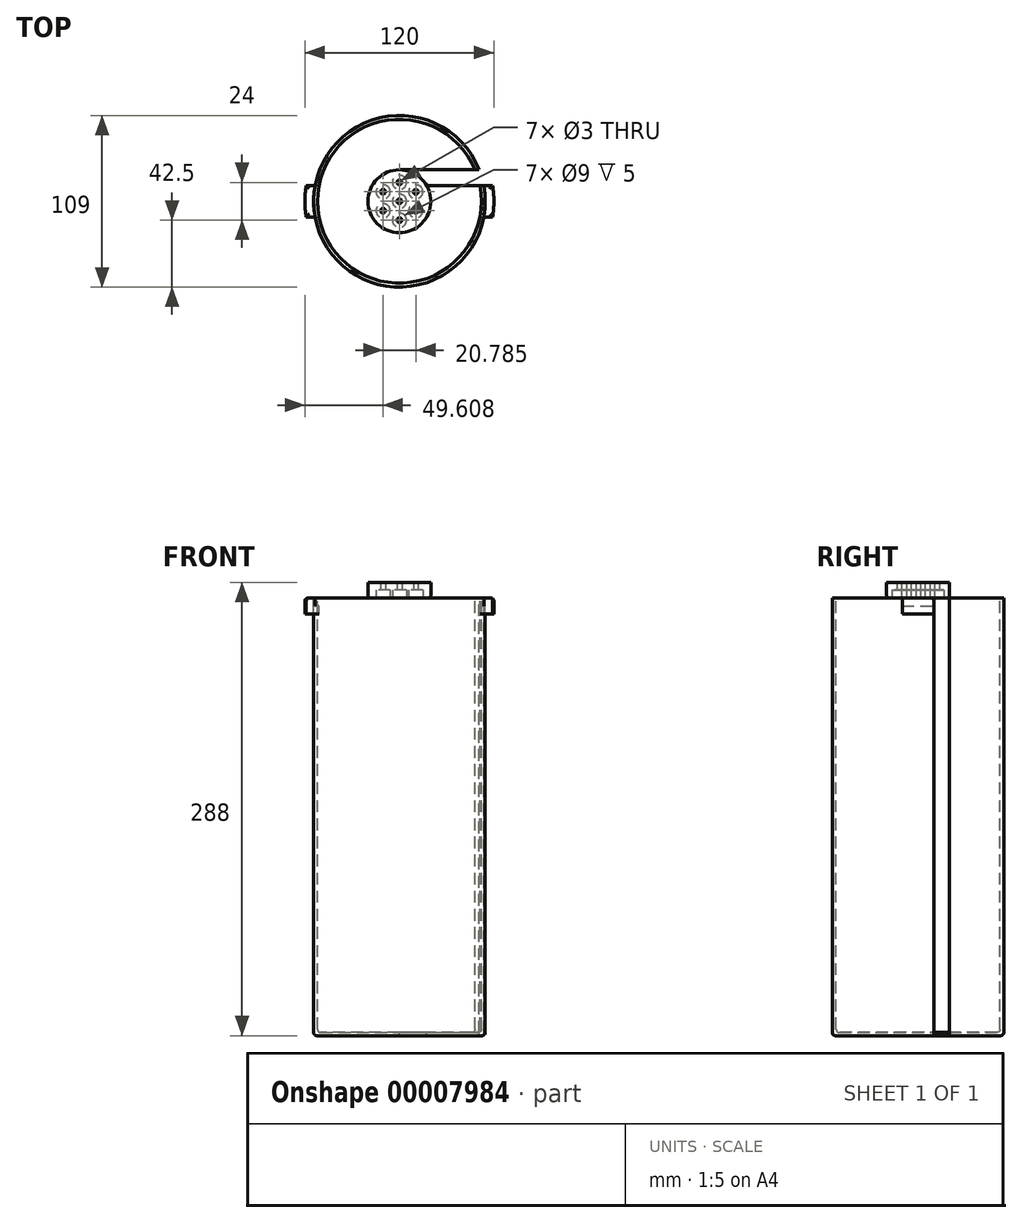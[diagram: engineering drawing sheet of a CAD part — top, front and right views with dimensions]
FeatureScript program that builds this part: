
annotation { "Feature Type Name" : "Feature", "Feature Type Description" : "" }
export const myFeature = defineFeature(function(context is Context, id is Id, definition is map)
    precondition{}
    {
        {
            var Q0;
            Q0=qCreatedBy(makeId("Top.planeOp"),FACE);
            var sketch = newSketch(context, id + "F0", { "sketchPlane" : qUnion([Q0])});
            skCircle(sketch, "E0", {"center": v(0, 0) * mm, "radius": 52 * mm});
            skCircle(sketch, "E1", {"center": v(0, 0) * mm, "radius": 4.5 * mm});
            skCircle(sketch, "E2", {"center": v(0, 12) * mm, "radius": 4.5 * mm});
            skLineSegment(sketch, "E3", {"start": v(0, 0) * mm, "end": v(0, 33.04) * mm, "construction": true});
            skCircle(sketch, "E4.1.0", {"center": v(-10.4, 6) * mm, "radius": 4.5 * mm});
            skCircle(sketch, "E4.2.0", {"center": v(-10.4, -6) * mm, "radius": 4.5 * mm});
            skCircle(sketch, "E4.3.0", {"center": v(0, -12) * mm, "radius": 4.5 * mm});
            skCircle(sketch, "E4.4.0", {"center": v(10.4, -6) * mm, "radius": 4.5 * mm});
            skCircle(sketch, "E4.5.0", {"center": v(10.4, 6) * mm, "radius": 4.5 * mm});
            skCircle(sketch, "E5", {"center": v(0, 0) * mm, "radius": 7.5 * mm, "construction": true});
            skCircle(sketch, "E6", {"center": v(0, 0) * mm, "radius": 20 * mm});
            skLineSegment(sketch, "E7.bottom", {"start": v(-65.9, 20) * mm, "end": v(65.9, 20) * mm});
            skLineSegment(sketch, "E7.top", {"start": v(-65.9, -20) * mm, "end": v(65.9, -20) * mm});
            skLineSegment(sketch, "E7.left", {"start": v(-65.9, 20) * mm, "end": v(-65.9, -20) * mm});
            skLineSegment(sketch, "E7.right", {"start": v(65.9, 20) * mm, "end": v(65.9, -20) * mm});
            skLineSegment(sketch, "E8", {"start": v(-65.9, 0) * mm, "end": v(65.9, 0) * mm, "construction": true});
            skCircle(sketch, "E9", {"center": v(0, 0) * mm, "radius": 54.5 * mm});
            skLineSegment(sketch, "E10", {"start": v(0, 20) * mm, "end": v(0, -20) * mm, "construction": true});
            skCircle(sketch, "E11", {"center": v(0, 0) * mm, "radius": 60 * mm});
            skCircle(sketch, "E12", {"center": v(0, 12) * mm, "radius": 1.5 * mm});
            skCircle(sketch, "E13", {"center": v(10.4, 6) * mm, "radius": 1.5 * mm});
            skCircle(sketch, "E14", {"center": v(10.4, -6) * mm, "radius": 1.5 * mm});
            skCircle(sketch, "E15", {"center": v(0, -12) * mm, "radius": 1.5 * mm});
            skCircle(sketch, "E16", {"center": v(-10.4, 6) * mm, "radius": 1.5 * mm});
            skCircle(sketch, "E17", {"center": v(-10.4, -6) * mm, "radius": 1.5 * mm});
            skCircle(sketch, "E18", {"center": v(0, 0) * mm, "radius": 1.5 * mm});
            skLineSegment(sketch, "E19.bottom", {"start": v(-65.9, -10) * mm, "end": v(-17.32, -10) * mm});
            skLineSegment(sketch, "E19.top", {"start": v(-65.9, 10) * mm, "end": v(-17.32, 10) * mm});
            skLineSegment(sketch, "E19.left", {"start": v(-65.9, -10) * mm, "end": v(-65.9, 10) * mm});
            skLineSegment(sketch, "E19.right", {"start": v(65.9, -10) * mm, "end": v(65.9, 10) * mm});
            skLineSegment(sketch, "E20.trimOffspring", {"start": v(17.32, -10) * mm, "end": v(65.9, -10) * mm});
            skLineSegment(sketch, "E21.trimOffspring", {"start": v(17.32, 10) * mm, "end": v(65.9, 10) * mm});
            skSolve(sketch);
        }
        {
            var Q0;
            {var subQ0=sQuery(id+"F0.wireOp",EDGE,"E19.top");var subQ1=sQuery(id+"F0.wireOp",EDGE,"E9");var subQ2=makeQuery(id+"F0.imprint","INTERSECT",VERTEX,{"disambiguationData":[OD(1.0)],"derivedFrom":[subQ1,subQ0]});Q0=makeQuery(id+"F0.imprint","IMPRINT",FACE,{"disambiguationData":[TD([[makeQuery(id+"F0.imprint","IMPRINT",EDGE,{"disambiguationData":[TD([[subQ2,-1.0]])],"derivedFrom":subQ1}),-1.0]])]});}
            var Q1;
            {var subQ0=sQuery(id+"F0.wireOp",EDGE,"E19.top");var subQ1=sQuery(id+"F0.wireOp",EDGE,"E0");var subQ2=makeQuery(id+"F0.imprint","INTERSECT",VERTEX,{"disambiguationData":[OD(1.0)],"derivedFrom":[subQ1,subQ0]});Q1=makeQuery(id+"F0.imprint","IMPRINT",FACE,{"disambiguationData":[TD([[makeQuery(id+"F0.imprint","IMPRINT",EDGE,{"disambiguationData":[TD([[subQ2,-1.0]])],"derivedFrom":subQ1}),-1.0]])]});}
            var Q2;
            {var subQ0=sQuery(id+"F0.wireOp",EDGE,"E19.top");var subQ1=sQuery(id+"F0.wireOp",EDGE,"E0");var subQ2=makeQuery(id+"F0.imprint","INTERSECT",VERTEX,{"disambiguationData":[OD(1.0)],"derivedFrom":[subQ1,subQ0]});Q2=makeQuery(id+"F0.imprint","IMPRINT",FACE,{"disambiguationData":[TD([[makeQuery(id+"F0.imprint","IMPRINT",EDGE,{"disambiguationData":[TD([[subQ2,-1.0]])],"derivedFrom":subQ1}),1.0]])]});}
            var Q3;
            Q3=makeQuery(id+"F0.imprint","IMPRINT",FACE,{"disambiguationData":[TD([[makeQuery(id+"F0.imprint","IMPRINT",EDGE,{"derivedFrom":sQuery(id+"F0.wireOp",EDGE,"E1")}),-1.0]])]});
            var Q4;
            {var subQ0=sQuery(id+"F0.wireOp",EDGE,"E19.bottom");var subQ7=sQuery(id+"F0.wireOp",EDGE,"E4.2.0");var subQ8=makeQuery(id+"F0.imprint","INTERSECT",VERTEX,{"disambiguationData":[OD(0.0)],"derivedFrom":[subQ7,subQ0]});Q4=makeQuery(id+"F0.imprint","IMPRINT",FACE,{"disambiguationData":[TD([[makeQuery(id+"F0.imprint","IMPRINT",EDGE,{"disambiguationData":[TD([[subQ8,-1.0]])],"derivedFrom":subQ7}),-1.0]])]});}
            var Q5;
            {var subQ2=sQuery(id+"F0.wireOp",EDGE,"E19.top");var subQ10=sQuery(id+"F0.wireOp",EDGE,"E2");var subQ11=makeQuery(id+"F0.imprint","INTERSECT",VERTEX,{"disambiguationData":[OD(0.0)],"derivedFrom":[subQ10,subQ2]});Q5=makeQuery(id+"F0.imprint","IMPRINT",FACE,{"disambiguationData":[TD([[makeQuery(id+"F0.imprint","IMPRINT",EDGE,{"disambiguationData":[TD([[subQ11,1.0]])],"derivedFrom":subQ10}),-1.0]])]});}
            var Q6;
            {var subQ0=sQuery(id+"F0.wireOp",EDGE,"E21.trimOffspring");var subQ1=sQuery(id+"F0.wireOp",EDGE,"E0");var subQ2=makeQuery(id+"F0.imprint","INTERSECT",VERTEX,{"derivedFrom":[subQ1,subQ0]});Q6=makeQuery(id+"F0.imprint","IMPRINT",FACE,{"disambiguationData":[TD([[makeQuery(id+"F0.imprint","IMPRINT",EDGE,{"disambiguationData":[TD([[subQ2,1.0]])],"derivedFrom":subQ1}),1.0]])]});}
            var Q7;
            {var subQ0=sQuery(id+"F0.wireOp",EDGE,"E21.trimOffspring");var subQ1=sQuery(id+"F0.wireOp",EDGE,"E0");var subQ2=makeQuery(id+"F0.imprint","INTERSECT",VERTEX,{"derivedFrom":[subQ1,subQ0]});Q7=makeQuery(id+"F0.imprint","IMPRINT",FACE,{"disambiguationData":[TD([[makeQuery(id+"F0.imprint","IMPRINT",EDGE,{"disambiguationData":[TD([[subQ2,1.0]])],"derivedFrom":subQ1}),-1.0]])]});}
            var Q8;
            {var subQ0=sQuery(id+"F0.wireOp",EDGE,"E21.trimOffspring");var subQ1=sQuery(id+"F0.wireOp",EDGE,"E9");var subQ2=makeQuery(id+"F0.imprint","INTERSECT",VERTEX,{"derivedFrom":[subQ1,subQ0]});Q8=makeQuery(id+"F0.imprint","IMPRINT",FACE,{"disambiguationData":[TD([[makeQuery(id+"F0.imprint","IMPRINT",EDGE,{"disambiguationData":[TD([[subQ2,1.0]])],"derivedFrom":subQ1}),-1.0]])]});}
            var Q9;
            Q9=makeQuery(id+"F0.imprint","IMPRINT",FACE,{"disambiguationData":[TD([[makeQuery(id+"F0.imprint","IMPRINT",EDGE,{"derivedFrom":sQuery(id+"F0.wireOp",EDGE,"E4.2.0")}),1.0]])]});
            var Q10;
            Q10=makeQuery(id+"F0.imprint","IMPRINT",FACE,{"disambiguationData":[TD([[makeQuery(id+"F0.imprint","IMPRINT",EDGE,{"derivedFrom":sQuery(id+"F0.wireOp",EDGE,"E4.3.0")}),1.0]])]});
            var Q11;
            Q11=makeQuery(id+"F0.imprint","IMPRINT",FACE,{"disambiguationData":[TD([[makeQuery(id+"F0.imprint","IMPRINT",EDGE,{"derivedFrom":sQuery(id+"F0.wireOp",EDGE,"E4.4.0")}),1.0]])]});
            var Q12;
            Q12=makeQuery(id+"F0.imprint","IMPRINT",FACE,{"disambiguationData":[TD([[makeQuery(id+"F0.imprint","IMPRINT",EDGE,{"derivedFrom":sQuery(id+"F0.wireOp",EDGE,"E4.5.0")}),1.0]])]});
            var Q13;
            Q13=makeQuery(id+"F0.imprint","IMPRINT",FACE,{"disambiguationData":[TD([[makeQuery(id+"F0.imprint","IMPRINT",EDGE,{"derivedFrom":sQuery(id+"F0.wireOp",EDGE,"E1")}),1.0]])]});
            var Q14;
            Q14=makeQuery(id+"F0.imprint","IMPRINT",FACE,{"disambiguationData":[TD([[makeQuery(id+"F0.imprint","IMPRINT",EDGE,{"derivedFrom":sQuery(id+"F0.wireOp",EDGE,"E4.1.0")}),1.0]])]});
            var Q15;
            Q15=makeQuery(id+"F0.imprint","IMPRINT",FACE,{"disambiguationData":[TD([[makeQuery(id+"F0.imprint","IMPRINT",EDGE,{"derivedFrom":sQuery(id+"F0.wireOp",EDGE,"E2")}),1.0]])]});
            extrude(context, id + "F1", {"entities" : qUnion([Q0, Q1, Q2, Q3, Q4, Q5, Q6, Q7, Q8, Q9, Q10, Q11, Q12, Q13, Q14, Q15]), "oppositeDirection" : true, "depth" : 10 * mm});
        }
        {
            var Q0;
            Q0=makeQuery(id+"F0.imprint","IMPRINT",FACE,{"disambiguationData":[TD([[makeQuery(id+"F0.imprint","IMPRINT",EDGE,{"derivedFrom":sQuery(id+"F0.wireOp",EDGE,"E4.4.0")}),1.0]])]});
            var Q1;
            Q1=makeQuery(id+"F0.imprint","IMPRINT",FACE,{"disambiguationData":[TD([[makeQuery(id+"F0.imprint","IMPRINT",EDGE,{"derivedFrom":sQuery(id+"F0.wireOp",EDGE,"E4.3.0")}),1.0]])]});
            var Q2;
            Q2=makeQuery(id+"F0.imprint","IMPRINT",FACE,{"disambiguationData":[TD([[makeQuery(id+"F0.imprint","IMPRINT",EDGE,{"derivedFrom":sQuery(id+"F0.wireOp",EDGE,"E4.1.0")}),1.0]])]});
            var Q3;
            Q3=makeQuery(id+"F0.imprint","IMPRINT",FACE,{"disambiguationData":[TD([[makeQuery(id+"F0.imprint","IMPRINT",EDGE,{"derivedFrom":sQuery(id+"F0.wireOp",EDGE,"E2")}),1.0]])]});
            var Q4;
            Q4=makeQuery(id+"F0.imprint","IMPRINT",FACE,{"disambiguationData":[TD([[makeQuery(id+"F0.imprint","IMPRINT",EDGE,{"derivedFrom":sQuery(id+"F0.wireOp",EDGE,"E1")}),1.0]])]});
            var Q5;
            Q5=makeQuery(id+"F0.imprint","IMPRINT",FACE,{"disambiguationData":[TD([[makeQuery(id+"F0.imprint","IMPRINT",EDGE,{"derivedFrom":sQuery(id+"F0.wireOp",EDGE,"E4.5.0")}),1.0]])]});
            var Q6;
            Q6=makeQuery(id+"F0.imprint","IMPRINT",FACE,{"disambiguationData":[TD([[makeQuery(id+"F0.imprint","IMPRINT",EDGE,{"derivedFrom":sQuery(id+"F0.wireOp",EDGE,"E4.2.0")}),1.0]])]});
            var Q7;
            {var subQ0=sQuery(id+"F0.wireOp",EDGE,"E19.top");var subQ1=sQuery(id+"F0.wireOp",EDGE,"E0");var subQ2=makeQuery(id+"F0.imprint","INTERSECT",VERTEX,{"derivedFrom":[subQ1,subQ0]});Q7=makeQuery(id+"F0.imprint","IMPRINT",FACE,{"disambiguationData":[TD([[makeQuery(id+"F0.imprint","IMPRINT",EDGE,{"disambiguationData":[TD([[subQ2,-1.0]])],"derivedFrom":subQ1}),-1.0]])]});}
            var Q8;
            {var subQ0=sQuery(id+"F0.wireOp",EDGE,"E21.trimOffspring");var subQ1=sQuery(id+"F0.wireOp",EDGE,"E0");var subQ2=makeQuery(id+"F0.imprint","INTERSECT",VERTEX,{"derivedFrom":[subQ1,subQ0]});Q8=makeQuery(id+"F0.imprint","IMPRINT",FACE,{"disambiguationData":[TD([[makeQuery(id+"F0.imprint","IMPRINT",EDGE,{"disambiguationData":[TD([[subQ2,1.0]])],"derivedFrom":subQ1}),-1.0]])]});}
            extrude(context, id + "F2", {"entities" : qUnion([Q0, Q1, Q2, Q3, Q4, Q5, Q6, Q7, Q8]), "operationType" : NewBodyOperationType.REMOVE, "oppositeDirection" : true, "depth" : 5 * mm});
        }
        {
            var Q0;
            {var subQ0=sQuery(id+"F0.wireOp",EDGE,"E6");Q0=makeQuery(id+"F1.opExtrude","CAP_EDGE",EDGE,{"disambiguationData":[OSD([subQ0]),TDD([makeQuery(id+"F0.imprint","IMPRINT",EDGE,{"disambiguationData":[TD([[makeQuery(id+"F0.imprint","INTERSECT",VERTEX,{"derivedFrom":[subQ0,sQuery(id+"F0.wireOp",EDGE,"E19.bottom")]}),-1.0]])],"derivedFrom":subQ0}),makeQuery(id+"F0.imprint","IMPRINT",EDGE,{"disambiguationData":[TD([[makeQuery(id+"F0.imprint","INTERSECT",VERTEX,{"derivedFrom":[subQ0,sQuery(id+"F0.wireOp",EDGE,"E20.trimOffspring")]}),1.0]])],"derivedFrom":subQ0})])],"isStart":true});}
            var Q1;
            {var subQ0=sQuery(id+"F0.wireOp",EDGE,"E21.trimOffspring");var subQ1=sQuery(id+"F0.wireOp",EDGE,"E20.trimOffspring");var subQ5=sQuery(id+"F0.wireOp",EDGE,"E0");Q1=makeQuery(id+"F2.boolean.opBoolean","SPLIT",EDGE,{"disambiguationData":[TD([makeQuery(id+"F2.opExtrude","SWEPT_FACE",FACE,{"disambiguationData":[OSD([subQ5]),TDD([makeQuery(id+"F0.imprint","IMPRINT",EDGE,{"disambiguationData":[TD([[makeQuery(id+"F0.imprint","INTERSECT",VERTEX,{"derivedFrom":[subQ5,subQ0]}),1.0]])],"derivedFrom":subQ5})])]})])],"derivedFrom":makeQuery(id+"F1.opExtrude","CAP_EDGE",EDGE,{"disambiguationData":[OSD([subQ1])],"isStart":true})});}
            var Q2;
            {var subQ0=sQuery(id+"F0.wireOp",EDGE,"E21.trimOffspring");var subQ1=sQuery(id+"F0.wireOp",EDGE,"E20.trimOffspring");var subQ2=sQuery(id+"F0.wireOp",EDGE,"E11");Q2=makeQuery(id+"F2.boolean.opBoolean","SPLIT",EDGE,{"disambiguationData":[TD([makeQuery(id+"F1.opExtrude","SWEPT_FACE",FACE,{"disambiguationData":[OSD([subQ2]),TDD([makeQuery(id+"F0.imprint","IMPRINT",EDGE,{"disambiguationData":[TD([[makeQuery(id+"F0.imprint","INTERSECT",VERTEX,{"derivedFrom":[subQ2,subQ0]}),1.0]])],"derivedFrom":subQ2})])]})])],"derivedFrom":makeQuery(id+"F1.opExtrude","CAP_EDGE",EDGE,{"disambiguationData":[OSD([subQ1])],"isStart":true})});}
            var Q3;
            {var subQ0=sQuery(id+"F0.wireOp",EDGE,"E11");Q3=makeQuery(id+"F1.opExtrude","CAP_EDGE",EDGE,{"disambiguationData":[OSD([subQ0]),TDD([makeQuery(id+"F0.imprint","IMPRINT",EDGE,{"disambiguationData":[TD([[makeQuery(id+"F0.imprint","INTERSECT",VERTEX,{"derivedFrom":[subQ0,sQuery(id+"F0.wireOp",EDGE,"E21.trimOffspring")]}),1.0]])],"derivedFrom":subQ0})])],"isStart":true});}
            var Q4;
            {var subQ3=sQuery(id+"F0.wireOp",EDGE,"E21.trimOffspring");var subQ5=sQuery(id+"F0.wireOp",EDGE,"E0");Q4=makeQuery(id+"F2.boolean.opBoolean","SPLIT",EDGE,{"disambiguationData":[TD([makeQuery(id+"F2.opExtrude","SWEPT_FACE",FACE,{"disambiguationData":[OSD([subQ5]),TDD([makeQuery(id+"F0.imprint","IMPRINT",EDGE,{"disambiguationData":[TD([[makeQuery(id+"F0.imprint","INTERSECT",VERTEX,{"derivedFrom":[subQ5,subQ3]}),1.0]])],"derivedFrom":subQ5})])]})])],"derivedFrom":makeQuery(id+"F1.opExtrude","CAP_EDGE",EDGE,{"disambiguationData":[OSD([subQ3])],"isStart":true})});}
            var Q5;
            {var subQ0=sQuery(id+"F0.wireOp",EDGE,"E21.trimOffspring");var subQ2=sQuery(id+"F0.wireOp",EDGE,"E11");Q5=makeQuery(id+"F2.boolean.opBoolean","SPLIT",EDGE,{"disambiguationData":[TD([makeQuery(id+"F1.opExtrude","SWEPT_FACE",FACE,{"disambiguationData":[OSD([subQ2]),TDD([makeQuery(id+"F0.imprint","IMPRINT",EDGE,{"disambiguationData":[TD([[makeQuery(id+"F0.imprint","INTERSECT",VERTEX,{"derivedFrom":[subQ2,subQ0]}),1.0]])],"derivedFrom":subQ2})])]})])],"derivedFrom":makeQuery(id+"F1.opExtrude","CAP_EDGE",EDGE,{"disambiguationData":[OSD([subQ0])],"isStart":true})});}
            var Q6;
            {var subQ0=sQuery(id+"F0.wireOp",EDGE,"E6");Q6=makeQuery(id+"F1.opExtrude","CAP_EDGE",EDGE,{"disambiguationData":[OSD([subQ0]),TDD([makeQuery(id+"F0.imprint","IMPRINT",EDGE,{"disambiguationData":[TD([[makeQuery(id+"F0.imprint","INTERSECT",VERTEX,{"derivedFrom":[subQ0,sQuery(id+"F0.wireOp",EDGE,"E21.trimOffspring")]}),-1.0]])],"derivedFrom":subQ0}),makeQuery(id+"F0.imprint","IMPRINT",EDGE,{"disambiguationData":[TD([[makeQuery(id+"F0.imprint","INTERSECT",VERTEX,{"derivedFrom":[subQ0,sQuery(id+"F0.wireOp",EDGE,"E19.top")]}),1.0]])],"derivedFrom":subQ0})])],"isStart":true});}
            var Q7;
            {var subQ0=sQuery(id+"F0.wireOp",EDGE,"E19.top");var subQ5=sQuery(id+"F0.wireOp",EDGE,"E0");Q7=makeQuery(id+"F2.boolean.opBoolean","SPLIT",EDGE,{"disambiguationData":[TD([makeQuery(id+"F2.opExtrude","SWEPT_FACE",FACE,{"disambiguationData":[OSD([subQ5]),TDD([makeQuery(id+"F0.imprint","IMPRINT",EDGE,{"disambiguationData":[TD([[makeQuery(id+"F0.imprint","INTERSECT",VERTEX,{"derivedFrom":[subQ5,subQ0]}),-1.0]])],"derivedFrom":subQ5})])]})])],"derivedFrom":makeQuery(id+"F1.opExtrude","CAP_EDGE",EDGE,{"disambiguationData":[OSD([subQ0])],"isStart":true})});}
            var Q8;
            {var subQ0=sQuery(id+"F0.wireOp",EDGE,"E19.top");var subQ2=sQuery(id+"F0.wireOp",EDGE,"E11");Q8=makeQuery(id+"F2.boolean.opBoolean","SPLIT",EDGE,{"disambiguationData":[TD([makeQuery(id+"F1.opExtrude","SWEPT_FACE",FACE,{"disambiguationData":[OSD([subQ2]),TDD([makeQuery(id+"F0.imprint","IMPRINT",EDGE,{"disambiguationData":[TD([[makeQuery(id+"F0.imprint","INTERSECT",VERTEX,{"derivedFrom":[subQ2,subQ0]}),-1.0]])],"derivedFrom":subQ2})])]})])],"derivedFrom":makeQuery(id+"F1.opExtrude","CAP_EDGE",EDGE,{"disambiguationData":[OSD([subQ0])],"isStart":true})});}
            var Q9;
            {var subQ0=sQuery(id+"F0.wireOp",EDGE,"E11");Q9=makeQuery(id+"F1.opExtrude","CAP_EDGE",EDGE,{"disambiguationData":[OSD([subQ0]),TDD([makeQuery(id+"F0.imprint","IMPRINT",EDGE,{"disambiguationData":[TD([[makeQuery(id+"F0.imprint","INTERSECT",VERTEX,{"derivedFrom":[subQ0,sQuery(id+"F0.wireOp",EDGE,"E19.top")]}),-1.0]])],"derivedFrom":subQ0})])],"isStart":true});}
            var Q10;
            {var subQ0=sQuery(id+"F0.wireOp",EDGE,"E19.top");var subQ1=sQuery(id+"F0.wireOp",EDGE,"E19.bottom");var subQ2=sQuery(id+"F0.wireOp",EDGE,"E11");Q10=makeQuery(id+"F2.boolean.opBoolean","SPLIT",EDGE,{"disambiguationData":[TD([makeQuery(id+"F1.opExtrude","SWEPT_FACE",FACE,{"disambiguationData":[OSD([subQ2]),TDD([makeQuery(id+"F0.imprint","IMPRINT",EDGE,{"disambiguationData":[TD([[makeQuery(id+"F0.imprint","INTERSECT",VERTEX,{"derivedFrom":[subQ2,subQ0]}),-1.0]])],"derivedFrom":subQ2})])]})])],"derivedFrom":makeQuery(id+"F1.opExtrude","CAP_EDGE",EDGE,{"disambiguationData":[OSD([subQ1])],"isStart":true})});}
            var Q11;
            {var subQ1=sQuery(id+"F0.wireOp",EDGE,"E19.top");var subQ2=sQuery(id+"F0.wireOp",EDGE,"E19.bottom");var subQ5=sQuery(id+"F0.wireOp",EDGE,"E0");Q11=makeQuery(id+"F2.boolean.opBoolean","SPLIT",EDGE,{"disambiguationData":[TD([makeQuery(id+"F2.opExtrude","SWEPT_FACE",FACE,{"disambiguationData":[OSD([subQ5]),TDD([makeQuery(id+"F0.imprint","IMPRINT",EDGE,{"disambiguationData":[TD([[makeQuery(id+"F0.imprint","INTERSECT",VERTEX,{"derivedFrom":[subQ5,subQ1]}),-1.0]])],"derivedFrom":subQ5})])]})])],"derivedFrom":makeQuery(id+"F1.opExtrude","CAP_EDGE",EDGE,{"disambiguationData":[OSD([subQ2])],"isStart":true})});}
            fillet(context, id + "F3", {"entities" : qUnion([Q0, Q1, Q2, Q3, Q4, Q5, Q6, Q7, Q8, Q9, Q10, Q11]), "radius" : 2 * mm, "tangentPropagation" : true, "allowEdgeOverflow" : false});
        }
        {
            var Q0;
            Q0=makeQuery(id+"F0.imprint","IMPRINT",FACE,{"disambiguationData":[TD([[makeQuery(id+"F0.imprint","IMPRINT",EDGE,{"derivedFrom":sQuery(id+"F0.wireOp",EDGE,"E1")}),-1.0]])]});
            var Q1;
            Q1=makeQuery(id+"F0.imprint","IMPRINT",FACE,{"disambiguationData":[TD([[makeQuery(id+"F0.imprint","IMPRINT",EDGE,{"derivedFrom":sQuery(id+"F0.wireOp",EDGE,"E4.4.0")}),1.0]])]});
            var Q2;
            Q2=makeQuery(id+"F0.imprint","IMPRINT",FACE,{"disambiguationData":[TD([[makeQuery(id+"F0.imprint","IMPRINT",EDGE,{"derivedFrom":sQuery(id+"F0.wireOp",EDGE,"E4.3.0")}),1.0]])]});
            var Q3;
            Q3=makeQuery(id+"F0.imprint","IMPRINT",FACE,{"disambiguationData":[TD([[makeQuery(id+"F0.imprint","IMPRINT",EDGE,{"derivedFrom":sQuery(id+"F0.wireOp",EDGE,"E4.2.0")}),1.0]])]});
            var Q4;
            Q4=makeQuery(id+"F0.imprint","IMPRINT",FACE,{"disambiguationData":[TD([[makeQuery(id+"F0.imprint","IMPRINT",EDGE,{"derivedFrom":sQuery(id+"F0.wireOp",EDGE,"E4.1.0")}),1.0]])]});
            var Q5;
            Q5=makeQuery(id+"F0.imprint","IMPRINT",FACE,{"disambiguationData":[TD([[makeQuery(id+"F0.imprint","IMPRINT",EDGE,{"derivedFrom":sQuery(id+"F0.wireOp",EDGE,"E2")}),1.0]])]});
            var Q6;
            Q6=makeQuery(id+"F0.imprint","IMPRINT",FACE,{"disambiguationData":[TD([[makeQuery(id+"F0.imprint","IMPRINT",EDGE,{"derivedFrom":sQuery(id+"F0.wireOp",EDGE,"E4.5.0")}),1.0]])]});
            var Q7;
            Q7=makeQuery(id+"F0.imprint","IMPRINT",FACE,{"disambiguationData":[TD([[makeQuery(id+"F0.imprint","IMPRINT",EDGE,{"derivedFrom":sQuery(id+"F0.wireOp",EDGE,"E1")}),1.0]])]});
            extrude(context, id + "F4", {"entities" : qUnion([Q0, Q1, Q2, Q3, Q4, Q5, Q6, Q7]), "depth" : 10 * mm});
        }
        {
            var Q0;
            Q0=makeQuery(id+"F0.imprint","IMPRINT",FACE,{"disambiguationData":[TD([[makeQuery(id+"F0.imprint","IMPRINT",EDGE,{"derivedFrom":sQuery(id+"F0.wireOp",EDGE,"E4.5.0")}),1.0]])]});
            var Q1;
            Q1=makeQuery(id+"F0.imprint","IMPRINT",FACE,{"disambiguationData":[TD([[makeQuery(id+"F0.imprint","IMPRINT",EDGE,{"derivedFrom":sQuery(id+"F0.wireOp",EDGE,"E2")}),1.0]])]});
            var Q2;
            Q2=makeQuery(id+"F0.imprint","IMPRINT",FACE,{"disambiguationData":[TD([[makeQuery(id+"F0.imprint","IMPRINT",EDGE,{"derivedFrom":sQuery(id+"F0.wireOp",EDGE,"E4.1.0")}),1.0]])]});
            var Q3;
            Q3=makeQuery(id+"F0.imprint","IMPRINT",FACE,{"disambiguationData":[TD([[makeQuery(id+"F0.imprint","IMPRINT",EDGE,{"derivedFrom":sQuery(id+"F0.wireOp",EDGE,"E4.2.0")}),1.0]])]});
            var Q4;
            Q4=makeQuery(id+"F0.imprint","IMPRINT",FACE,{"disambiguationData":[TD([[makeQuery(id+"F0.imprint","IMPRINT",EDGE,{"derivedFrom":sQuery(id+"F0.wireOp",EDGE,"E4.3.0")}),1.0]])]});
            var Q5;
            Q5=makeQuery(id+"F0.imprint","IMPRINT",FACE,{"disambiguationData":[TD([[makeQuery(id+"F0.imprint","IMPRINT",EDGE,{"derivedFrom":sQuery(id+"F0.wireOp",EDGE,"E4.4.0")}),1.0]])]});
            var Q6;
            Q6=makeQuery(id+"F0.imprint","IMPRINT",FACE,{"disambiguationData":[TD([[makeQuery(id+"F0.imprint","IMPRINT",EDGE,{"derivedFrom":sQuery(id+"F0.wireOp",EDGE,"E1")}),1.0]])]});
            extrude(context, id + "F5", {"entities" : qUnion([Q0, Q1, Q2, Q3, Q4, Q5, Q6]), "operationType" : NewBodyOperationType.REMOVE, "depth" : 5 * mm});
        }
        {
            var Q0;
            Q0=makeQuery(id+"F4.opExtrude","CAP_EDGE",EDGE,{"disambiguationData":[OSD([sQuery(id+"F0.wireOp",EDGE,"E6")])],"isStart":true});
            fillet(context, id + "F6", {"entities" : qUnion([Q0]), "radius" : 2 * mm, "tangentPropagation" : true, "allowEdgeOverflow" : false});
        }
        {
            var Q0;
            {var subQ0=sQuery(id+"F0.wireOp",EDGE,"E7.bottom");var subQ1=sQuery(id+"F0.wireOp",EDGE,"E0");var subQ2=makeQuery(id+"F0.imprint","INTERSECT",VERTEX,{"disambiguationData":[OD(0.0)],"derivedFrom":[subQ1,subQ0]});Q0=makeQuery(id+"F0.imprint","IMPRINT",FACE,{"disambiguationData":[TD([[makeQuery(id+"F0.imprint","IMPRINT",EDGE,{"disambiguationData":[TD([[subQ2,-1.0]])],"derivedFrom":subQ1}),-1.0]])]});}
            var Q1;
            {var subQ0=sQuery(id+"F0.wireOp",EDGE,"E7.bottom");var subQ1=sQuery(id+"F0.wireOp",EDGE,"E0");var subQ2=makeQuery(id+"F0.imprint","INTERSECT",VERTEX,{"disambiguationData":[OD(1.0)],"derivedFrom":[subQ1,subQ0]});Q1=makeQuery(id+"F0.imprint","IMPRINT",FACE,{"disambiguationData":[TD([[makeQuery(id+"F0.imprint","IMPRINT",EDGE,{"disambiguationData":[TD([[subQ2,-1.0]])],"derivedFrom":subQ1}),-1.0]])]});}
            var Q2;
            {var subQ0=sQuery(id+"F0.wireOp",EDGE,"E19.top");var subQ1=sQuery(id+"F0.wireOp",EDGE,"E0");var subQ2=makeQuery(id+"F0.imprint","INTERSECT",VERTEX,{"derivedFrom":[subQ1,subQ0]});Q2=makeQuery(id+"F0.imprint","IMPRINT",FACE,{"disambiguationData":[TD([[makeQuery(id+"F0.imprint","IMPRINT",EDGE,{"disambiguationData":[TD([[subQ2,-1.0]])],"derivedFrom":subQ1}),-1.0]])]});}
            var Q3;
            {var subQ0=sQuery(id+"F0.wireOp",EDGE,"E19.bottom");var subQ1=sQuery(id+"F0.wireOp",EDGE,"E0");var subQ2=makeQuery(id+"F0.imprint","INTERSECT",VERTEX,{"derivedFrom":[subQ1,subQ0]});Q3=makeQuery(id+"F0.imprint","IMPRINT",FACE,{"disambiguationData":[TD([[makeQuery(id+"F0.imprint","IMPRINT",EDGE,{"disambiguationData":[TD([[subQ2,-1.0]])],"derivedFrom":subQ1}),-1.0]])]});}
            var Q4;
            {var subQ0=sQuery(id+"F0.wireOp",EDGE,"E7.top");var subQ1=sQuery(id+"F0.wireOp",EDGE,"E0");var subQ2=makeQuery(id+"F0.imprint","INTERSECT",VERTEX,{"disambiguationData":[OD(0.0)],"derivedFrom":[subQ1,subQ0]});Q4=makeQuery(id+"F0.imprint","IMPRINT",FACE,{"disambiguationData":[TD([[makeQuery(id+"F0.imprint","IMPRINT",EDGE,{"disambiguationData":[TD([[subQ2,-1.0]])],"derivedFrom":subQ1}),-1.0]])]});}
            var Q5;
            {var subQ0=sQuery(id+"F0.wireOp",EDGE,"E7.top");var subQ1=sQuery(id+"F0.wireOp",EDGE,"E0");var subQ2=makeQuery(id+"F0.imprint","INTERSECT",VERTEX,{"disambiguationData":[OD(1.0)],"derivedFrom":[subQ1,subQ0]});Q5=makeQuery(id+"F0.imprint","IMPRINT",FACE,{"disambiguationData":[TD([[makeQuery(id+"F0.imprint","IMPRINT",EDGE,{"disambiguationData":[TD([[subQ2,-1.0]])],"derivedFrom":subQ1}),-1.0]])]});}
            var Q6;
            {var subQ0=sQuery(id+"F0.wireOp",EDGE,"E21.trimOffspring");var subQ1=sQuery(id+"F0.wireOp",EDGE,"E0");var subQ2=makeQuery(id+"F0.imprint","INTERSECT",VERTEX,{"derivedFrom":[subQ1,subQ0]});Q6=makeQuery(id+"F0.imprint","IMPRINT",FACE,{"disambiguationData":[TD([[makeQuery(id+"F0.imprint","IMPRINT",EDGE,{"disambiguationData":[TD([[subQ2,1.0]])],"derivedFrom":subQ1}),-1.0]])]});}
            var Q7;
            {var subQ0=sQuery(id+"F0.wireOp",EDGE,"E7.bottom");var subQ1=sQuery(id+"F0.wireOp",EDGE,"E0");var subQ2=makeQuery(id+"F0.imprint","INTERSECT",VERTEX,{"disambiguationData":[OD(0.0)],"derivedFrom":[subQ1,subQ0]});Q7=makeQuery(id+"F0.imprint","IMPRINT",FACE,{"disambiguationData":[TD([[makeQuery(id+"F0.imprint","IMPRINT",EDGE,{"disambiguationData":[TD([[subQ2,1.0]])],"derivedFrom":subQ1}),-1.0]])]});}
            var Q8;
            {var subQ0=sQuery(id+"F0.wireOp",EDGE,"E19.top");var subQ1=sQuery(id+"F0.wireOp",EDGE,"E0");var subQ2=makeQuery(id+"F0.imprint","INTERSECT",VERTEX,{"derivedFrom":[subQ1,subQ0]});Q8=makeQuery(id+"F0.imprint","IMPRINT",FACE,{"disambiguationData":[TD([[makeQuery(id+"F0.imprint","IMPRINT",EDGE,{"disambiguationData":[TD([[subQ2,-1.0]])],"derivedFrom":subQ1}),1.0]])]});}
            var Q9;
            Q9=makeQuery(id+"F0.imprint","IMPRINT",FACE,{"disambiguationData":[TD([[makeQuery(id+"F0.imprint","IMPRINT",EDGE,{"derivedFrom":sQuery(id+"F0.wireOp",EDGE,"E4.2.0")}),1.0]])]});
            var Q10;
            {var subQ0=sQuery(id+"F0.wireOp",EDGE,"E7.bottom");var subQ1=sQuery(id+"F0.wireOp",EDGE,"E0");var subQ2=makeQuery(id+"F0.imprint","INTERSECT",VERTEX,{"disambiguationData":[OD(1.0)],"derivedFrom":[subQ1,subQ0]});Q10=makeQuery(id+"F0.imprint","IMPRINT",FACE,{"disambiguationData":[TD([[makeQuery(id+"F0.imprint","IMPRINT",EDGE,{"disambiguationData":[TD([[subQ2,-1.0]])],"derivedFrom":subQ1}),1.0]])]});}
            var Q11;
            {var subQ0=sQuery(id+"F0.wireOp",EDGE,"E7.bottom");var subQ1=sQuery(id+"F0.wireOp",EDGE,"E0");var subQ2=makeQuery(id+"F0.imprint","INTERSECT",VERTEX,{"disambiguationData":[OD(0.0)],"derivedFrom":[subQ1,subQ0]});Q11=makeQuery(id+"F0.imprint","IMPRINT",FACE,{"disambiguationData":[TD([[makeQuery(id+"F0.imprint","IMPRINT",EDGE,{"disambiguationData":[TD([[subQ2,-1.0]])],"derivedFrom":subQ1}),1.0]])]});}
            var Q12;
            {var subQ0=sQuery(id+"F0.wireOp",EDGE,"E19.bottom");var subQ1=sQuery(id+"F0.wireOp",EDGE,"E0");var subQ2=makeQuery(id+"F0.imprint","INTERSECT",VERTEX,{"derivedFrom":[subQ1,subQ0]});Q12=makeQuery(id+"F0.imprint","IMPRINT",FACE,{"disambiguationData":[TD([[makeQuery(id+"F0.imprint","IMPRINT",EDGE,{"disambiguationData":[TD([[subQ2,-1.0]])],"derivedFrom":subQ1}),1.0]])]});}
            var Q13;
            Q13=makeQuery(id+"F0.imprint","IMPRINT",FACE,{"disambiguationData":[TD([[makeQuery(id+"F0.imprint","IMPRINT",EDGE,{"derivedFrom":sQuery(id+"F0.wireOp",EDGE,"E17")}),1.0]])]});
            var Q14;
            {var subQ0=sQuery(id+"F0.wireOp",EDGE,"E7.top");var subQ1=sQuery(id+"F0.wireOp",EDGE,"E0");var subQ2=makeQuery(id+"F0.imprint","INTERSECT",VERTEX,{"disambiguationData":[OD(0.0)],"derivedFrom":[subQ1,subQ0]});Q14=makeQuery(id+"F0.imprint","IMPRINT",FACE,{"disambiguationData":[TD([[makeQuery(id+"F0.imprint","IMPRINT",EDGE,{"disambiguationData":[TD([[subQ2,-1.0]])],"derivedFrom":subQ1}),1.0]])]});}
            var Q15;
            {var subQ0=sQuery(id+"F0.wireOp",EDGE,"E7.bottom");var subQ1=sQuery(id+"F0.wireOp",EDGE,"E0");var subQ2=makeQuery(id+"F0.imprint","INTERSECT",VERTEX,{"disambiguationData":[OD(0.0)],"derivedFrom":[subQ1,subQ0]});Q15=makeQuery(id+"F0.imprint","IMPRINT",FACE,{"disambiguationData":[TD([[makeQuery(id+"F0.imprint","IMPRINT",EDGE,{"disambiguationData":[TD([[subQ2,1.0]])],"derivedFrom":subQ1}),1.0]])]});}
            var Q16;
            {var subQ0=sQuery(id+"F0.wireOp",EDGE,"E21.trimOffspring");var subQ1=sQuery(id+"F0.wireOp",EDGE,"E0");var subQ2=makeQuery(id+"F0.imprint","INTERSECT",VERTEX,{"derivedFrom":[subQ1,subQ0]});Q16=makeQuery(id+"F0.imprint","IMPRINT",FACE,{"disambiguationData":[TD([[makeQuery(id+"F0.imprint","IMPRINT",EDGE,{"disambiguationData":[TD([[subQ2,1.0]])],"derivedFrom":subQ1}),1.0]])]});}
            var Q17;
            {var subQ0=sQuery(id+"F0.wireOp",EDGE,"E7.top");var subQ1=sQuery(id+"F0.wireOp",EDGE,"E0");var subQ2=makeQuery(id+"F0.imprint","INTERSECT",VERTEX,{"disambiguationData":[OD(1.0)],"derivedFrom":[subQ1,subQ0]});Q17=makeQuery(id+"F0.imprint","IMPRINT",FACE,{"disambiguationData":[TD([[makeQuery(id+"F0.imprint","IMPRINT",EDGE,{"disambiguationData":[TD([[subQ2,-1.0]])],"derivedFrom":subQ1}),1.0]])]});}
            var Q18;
            Q18=makeQuery(id+"F0.imprint","IMPRINT",FACE,{"disambiguationData":[TD([[makeQuery(id+"F0.imprint","IMPRINT",EDGE,{"derivedFrom":sQuery(id+"F0.wireOp",EDGE,"E1")}),-1.0]])]});
            var Q19;
            Q19=makeQuery(id+"F0.imprint","IMPRINT",FACE,{"disambiguationData":[TD([[makeQuery(id+"F0.imprint","IMPRINT",EDGE,{"derivedFrom":sQuery(id+"F0.wireOp",EDGE,"E4.1.0")}),1.0]])]});
            var Q20;
            Q20=makeQuery(id+"F0.imprint","IMPRINT",FACE,{"disambiguationData":[TD([[makeQuery(id+"F0.imprint","IMPRINT",EDGE,{"derivedFrom":sQuery(id+"F0.wireOp",EDGE,"E2")}),1.0]])]});
            var Q21;
            Q21=makeQuery(id+"F0.imprint","IMPRINT",FACE,{"disambiguationData":[TD([[makeQuery(id+"F0.imprint","IMPRINT",EDGE,{"derivedFrom":sQuery(id+"F0.wireOp",EDGE,"E1")}),1.0]])]});
            var Q22;
            Q22=makeQuery(id+"F0.imprint","IMPRINT",FACE,{"disambiguationData":[TD([[makeQuery(id+"F0.imprint","IMPRINT",EDGE,{"derivedFrom":sQuery(id+"F0.wireOp",EDGE,"E4.5.0")}),1.0]])]});
            var Q23;
            Q23=makeQuery(id+"F0.imprint","IMPRINT",FACE,{"disambiguationData":[TD([[makeQuery(id+"F0.imprint","IMPRINT",EDGE,{"derivedFrom":sQuery(id+"F0.wireOp",EDGE,"E4.4.0")}),1.0]])]});
            var Q24;
            Q24=makeQuery(id+"F0.imprint","IMPRINT",FACE,{"disambiguationData":[TD([[makeQuery(id+"F0.imprint","IMPRINT",EDGE,{"derivedFrom":sQuery(id+"F0.wireOp",EDGE,"E4.3.0")}),1.0]])]});
            var Q25;
            Q25=makeQuery(id+"F0.imprint","IMPRINT",FACE,{"disambiguationData":[TD([[makeQuery(id+"F0.imprint","IMPRINT",EDGE,{"derivedFrom":sQuery(id+"F0.wireOp",EDGE,"E16")}),1.0]])]});
            var Q26;
            Q26=makeQuery(id+"F0.imprint","IMPRINT",FACE,{"disambiguationData":[TD([[makeQuery(id+"F0.imprint","IMPRINT",EDGE,{"derivedFrom":sQuery(id+"F0.wireOp",EDGE,"E12")}),1.0]])]});
            var Q27;
            Q27=makeQuery(id+"F0.imprint","IMPRINT",FACE,{"disambiguationData":[TD([[makeQuery(id+"F0.imprint","IMPRINT",EDGE,{"derivedFrom":sQuery(id+"F0.wireOp",EDGE,"E13")}),1.0]])]});
            var Q28;
            Q28=makeQuery(id+"F0.imprint","IMPRINT",FACE,{"disambiguationData":[TD([[makeQuery(id+"F0.imprint","IMPRINT",EDGE,{"derivedFrom":sQuery(id+"F0.wireOp",EDGE,"E14")}),1.0]])]});
            var Q29;
            Q29=makeQuery(id+"F0.imprint","IMPRINT",FACE,{"disambiguationData":[TD([[makeQuery(id+"F0.imprint","IMPRINT",EDGE,{"derivedFrom":sQuery(id+"F0.wireOp",EDGE,"E18")}),1.0]])]});
            var Q30;
            Q30=makeQuery(id+"F0.imprint","IMPRINT",FACE,{"disambiguationData":[TD([[makeQuery(id+"F0.imprint","IMPRINT",EDGE,{"derivedFrom":sQuery(id+"F0.wireOp",EDGE,"E15")}),1.0]])]});
            extrude(context, id + "F7", {"entities" : qUnion([Q0, Q1, Q2, Q3, Q4, Q5, Q6, Q7, Q8, Q9, Q10, Q11, Q12, Q13, Q14, Q15, Q16, Q17, Q18, Q19, Q20, Q21, Q22, Q23, Q24, Q25, Q26, Q27, Q28, Q29, Q30]), "oppositeDirection" : true, "depth" : 278 * mm});
        }
        {
            var Q0;
            {var subQ0=sQuery(id+"F0.wireOp",EDGE,"E7.bottom");var subQ1=sQuery(id+"F0.wireOp",EDGE,"E0");var subQ2=makeQuery(id+"F0.imprint","INTERSECT",VERTEX,{"disambiguationData":[OD(0.0)],"derivedFrom":[subQ1,subQ0]});Q0=makeQuery(id+"F0.imprint","IMPRINT",FACE,{"disambiguationData":[TD([[makeQuery(id+"F0.imprint","IMPRINT",EDGE,{"disambiguationData":[TD([[subQ2,-1.0]])],"derivedFrom":subQ1}),1.0]])]});}
            var Q1;
            {var subQ0=sQuery(id+"F0.wireOp",EDGE,"E7.bottom");var subQ1=sQuery(id+"F0.wireOp",EDGE,"E0");var subQ2=makeQuery(id+"F0.imprint","INTERSECT",VERTEX,{"disambiguationData":[OD(0.0)],"derivedFrom":[subQ1,subQ0]});Q1=makeQuery(id+"F0.imprint","IMPRINT",FACE,{"disambiguationData":[TD([[makeQuery(id+"F0.imprint","IMPRINT",EDGE,{"disambiguationData":[TD([[subQ2,1.0]])],"derivedFrom":subQ1}),1.0]])]});}
            var Q2;
            {var subQ0=sQuery(id+"F0.wireOp",EDGE,"E21.trimOffspring");var subQ1=sQuery(id+"F0.wireOp",EDGE,"E0");var subQ2=makeQuery(id+"F0.imprint","INTERSECT",VERTEX,{"derivedFrom":[subQ1,subQ0]});Q2=makeQuery(id+"F0.imprint","IMPRINT",FACE,{"disambiguationData":[TD([[makeQuery(id+"F0.imprint","IMPRINT",EDGE,{"disambiguationData":[TD([[subQ2,1.0]])],"derivedFrom":subQ1}),1.0]])]});}
            var Q3;
            {var subQ0=sQuery(id+"F0.wireOp",EDGE,"E7.top");var subQ1=sQuery(id+"F0.wireOp",EDGE,"E0");var subQ2=makeQuery(id+"F0.imprint","INTERSECT",VERTEX,{"disambiguationData":[OD(1.0)],"derivedFrom":[subQ1,subQ0]});Q3=makeQuery(id+"F0.imprint","IMPRINT",FACE,{"disambiguationData":[TD([[makeQuery(id+"F0.imprint","IMPRINT",EDGE,{"disambiguationData":[TD([[subQ2,-1.0]])],"derivedFrom":subQ1}),1.0]])]});}
            var Q4;
            {var subQ0=sQuery(id+"F0.wireOp",EDGE,"E7.top");var subQ1=sQuery(id+"F0.wireOp",EDGE,"E0");var subQ2=makeQuery(id+"F0.imprint","INTERSECT",VERTEX,{"disambiguationData":[OD(0.0)],"derivedFrom":[subQ1,subQ0]});Q4=makeQuery(id+"F0.imprint","IMPRINT",FACE,{"disambiguationData":[TD([[makeQuery(id+"F0.imprint","IMPRINT",EDGE,{"disambiguationData":[TD([[subQ2,-1.0]])],"derivedFrom":subQ1}),1.0]])]});}
            var Q5;
            {var subQ0=sQuery(id+"F0.wireOp",EDGE,"E19.bottom");var subQ1=sQuery(id+"F0.wireOp",EDGE,"E0");var subQ2=makeQuery(id+"F0.imprint","INTERSECT",VERTEX,{"derivedFrom":[subQ1,subQ0]});Q5=makeQuery(id+"F0.imprint","IMPRINT",FACE,{"disambiguationData":[TD([[makeQuery(id+"F0.imprint","IMPRINT",EDGE,{"disambiguationData":[TD([[subQ2,-1.0]])],"derivedFrom":subQ1}),1.0]])]});}
            var Q6;
            {var subQ0=sQuery(id+"F0.wireOp",EDGE,"E7.bottom");var subQ1=sQuery(id+"F0.wireOp",EDGE,"E0");var subQ2=makeQuery(id+"F0.imprint","INTERSECT",VERTEX,{"disambiguationData":[OD(1.0)],"derivedFrom":[subQ1,subQ0]});Q6=makeQuery(id+"F0.imprint","IMPRINT",FACE,{"disambiguationData":[TD([[makeQuery(id+"F0.imprint","IMPRINT",EDGE,{"disambiguationData":[TD([[subQ2,-1.0]])],"derivedFrom":subQ1}),1.0]])]});}
            var Q7;
            {var subQ0=sQuery(id+"F0.wireOp",EDGE,"E19.top");var subQ1=sQuery(id+"F0.wireOp",EDGE,"E0");var subQ2=makeQuery(id+"F0.imprint","INTERSECT",VERTEX,{"derivedFrom":[subQ1,subQ0]});Q7=makeQuery(id+"F0.imprint","IMPRINT",FACE,{"disambiguationData":[TD([[makeQuery(id+"F0.imprint","IMPRINT",EDGE,{"disambiguationData":[TD([[subQ2,-1.0]])],"derivedFrom":subQ1}),1.0]])]});}
            var Q8;
            Q8=makeQuery(id+"F0.imprint","IMPRINT",FACE,{"disambiguationData":[TD([[makeQuery(id+"F0.imprint","IMPRINT",EDGE,{"derivedFrom":sQuery(id+"F0.wireOp",EDGE,"E1")}),-1.0]])]});
            var Q9;
            Q9=makeQuery(id+"F0.imprint","IMPRINT",FACE,{"disambiguationData":[TD([[makeQuery(id+"F0.imprint","IMPRINT",EDGE,{"derivedFrom":sQuery(id+"F0.wireOp",EDGE,"E4.4.0")}),1.0]])]});
            var Q10;
            Q10=makeQuery(id+"F0.imprint","IMPRINT",FACE,{"disambiguationData":[TD([[makeQuery(id+"F0.imprint","IMPRINT",EDGE,{"derivedFrom":sQuery(id+"F0.wireOp",EDGE,"E14")}),1.0]])]});
            var Q11;
            Q11=makeQuery(id+"F0.imprint","IMPRINT",FACE,{"disambiguationData":[TD([[makeQuery(id+"F0.imprint","IMPRINT",EDGE,{"derivedFrom":sQuery(id+"F0.wireOp",EDGE,"E13")}),1.0]])]});
            var Q12;
            Q12=makeQuery(id+"F0.imprint","IMPRINT",FACE,{"disambiguationData":[TD([[makeQuery(id+"F0.imprint","IMPRINT",EDGE,{"derivedFrom":sQuery(id+"F0.wireOp",EDGE,"E4.5.0")}),1.0]])]});
            var Q13;
            Q13=makeQuery(id+"F0.imprint","IMPRINT",FACE,{"disambiguationData":[TD([[makeQuery(id+"F0.imprint","IMPRINT",EDGE,{"derivedFrom":sQuery(id+"F0.wireOp",EDGE,"E2")}),1.0]])]});
            var Q14;
            Q14=makeQuery(id+"F0.imprint","IMPRINT",FACE,{"disambiguationData":[TD([[makeQuery(id+"F0.imprint","IMPRINT",EDGE,{"derivedFrom":sQuery(id+"F0.wireOp",EDGE,"E12")}),1.0]])]});
            var Q15;
            Q15=makeQuery(id+"F0.imprint","IMPRINT",FACE,{"disambiguationData":[TD([[makeQuery(id+"F0.imprint","IMPRINT",EDGE,{"derivedFrom":sQuery(id+"F0.wireOp",EDGE,"E4.1.0")}),1.0]])]});
            var Q16;
            Q16=makeQuery(id+"F0.imprint","IMPRINT",FACE,{"disambiguationData":[TD([[makeQuery(id+"F0.imprint","IMPRINT",EDGE,{"derivedFrom":sQuery(id+"F0.wireOp",EDGE,"E16")}),1.0]])]});
            var Q17;
            Q17=makeQuery(id+"F0.imprint","IMPRINT",FACE,{"disambiguationData":[TD([[makeQuery(id+"F0.imprint","IMPRINT",EDGE,{"derivedFrom":sQuery(id+"F0.wireOp",EDGE,"E4.2.0")}),1.0]])]});
            var Q18;
            Q18=makeQuery(id+"F0.imprint","IMPRINT",FACE,{"disambiguationData":[TD([[makeQuery(id+"F0.imprint","IMPRINT",EDGE,{"derivedFrom":sQuery(id+"F0.wireOp",EDGE,"E17")}),1.0]])]});
            var Q19;
            Q19=makeQuery(id+"F0.imprint","IMPRINT",FACE,{"disambiguationData":[TD([[makeQuery(id+"F0.imprint","IMPRINT",EDGE,{"derivedFrom":sQuery(id+"F0.wireOp",EDGE,"E4.3.0")}),1.0]])]});
            var Q20;
            Q20=makeQuery(id+"F0.imprint","IMPRINT",FACE,{"disambiguationData":[TD([[makeQuery(id+"F0.imprint","IMPRINT",EDGE,{"derivedFrom":sQuery(id+"F0.wireOp",EDGE,"E15")}),1.0]])]});
            var Q21;
            Q21=makeQuery(id+"F0.imprint","IMPRINT",FACE,{"disambiguationData":[TD([[makeQuery(id+"F0.imprint","IMPRINT",EDGE,{"derivedFrom":sQuery(id+"F0.wireOp",EDGE,"E1")}),1.0]])]});
            var Q22;
            Q22=makeQuery(id+"F0.imprint","IMPRINT",FACE,{"disambiguationData":[TD([[makeQuery(id+"F0.imprint","IMPRINT",EDGE,{"derivedFrom":sQuery(id+"F0.wireOp",EDGE,"E18")}),1.0]])]});
            extrude(context, id + "F8", {"entities" : qUnion([Q0, Q1, Q2, Q3, Q4, Q5, Q6, Q7, Q8, Q9, Q10, Q11, Q12, Q13, Q14, Q15, Q16, Q17, Q18, Q19, Q20, Q21, Q22]), "operationType" : NewBodyOperationType.REMOVE, "oppositeDirection" : true, "depth" : 276 * mm});
        }
        {
            var Q0;
            Q0=makeQuery(id+"F8.boolean.opBoolean","COPY",EDGE,{"derivedFrom":makeQuery(id+"F8.opExtrude","CAP_EDGE",EDGE,{"disambiguationData":[OSD([sQuery(id+"F0.wireOp",EDGE,"E0")])],"isStart":false})});
            var Q1;
            Q1=makeQuery(id+"F7.opExtrude","CAP_EDGE",EDGE,{"disambiguationData":[OSD([sQuery(id+"F0.wireOp",EDGE,"E9")])],"isStart":false});
            fillet(context, id + "F9", {"entities" : qUnion([Q0, Q1]), "radius" : 2 * mm, "tangentPropagation" : true, "allowEdgeOverflow" : false});
        }
    });
